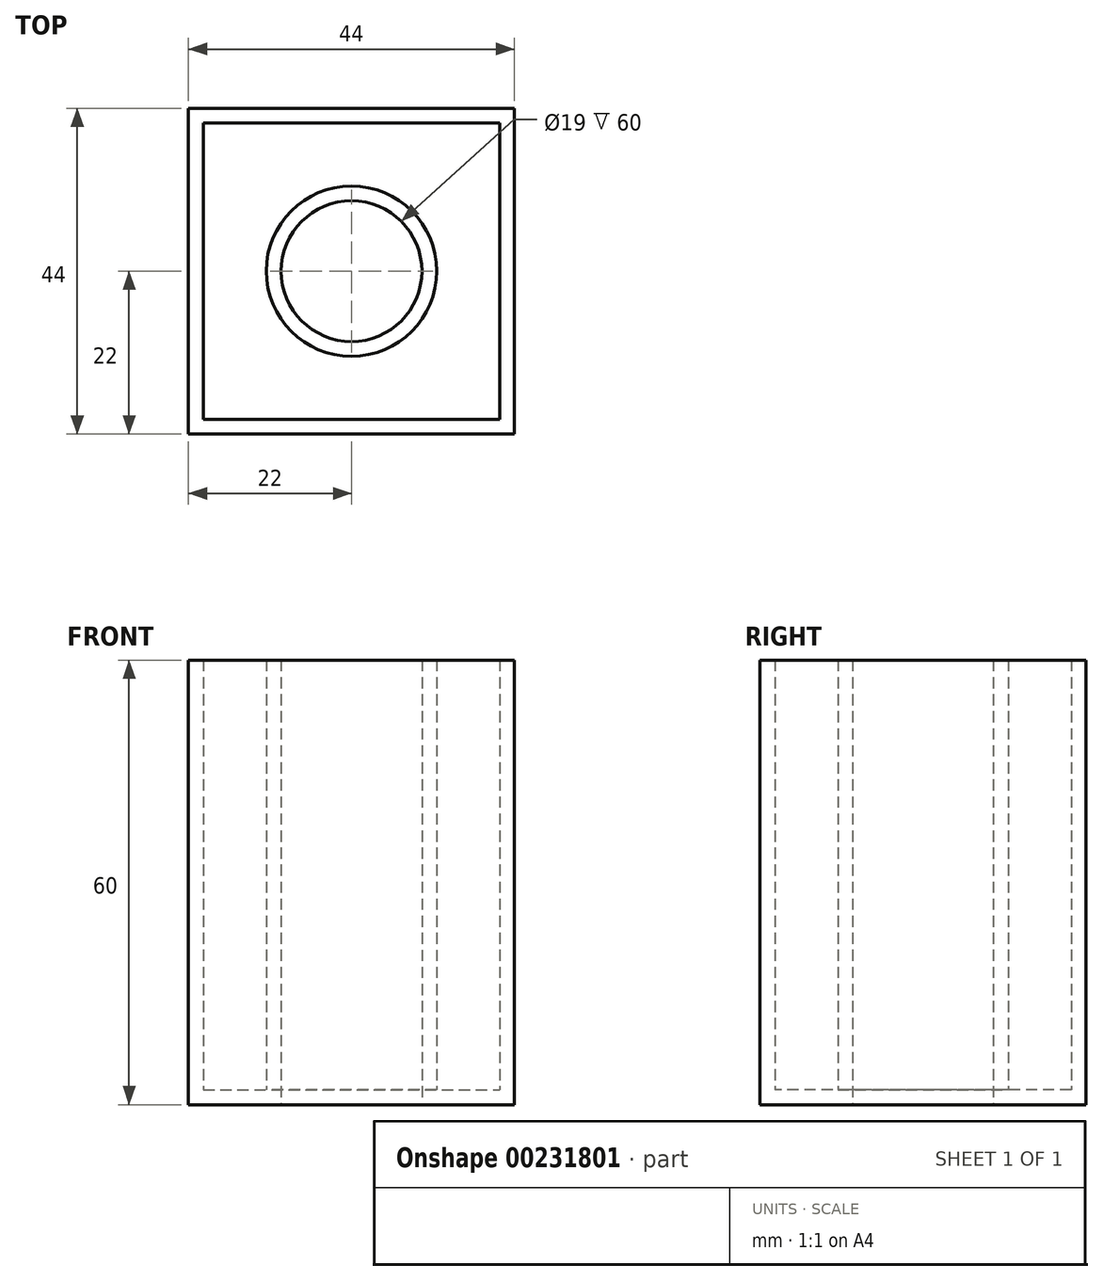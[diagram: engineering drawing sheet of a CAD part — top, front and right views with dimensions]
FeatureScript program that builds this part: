
annotation { "Feature Type Name" : "Feature", "Feature Type Description" : "" }
export const myFeature = defineFeature(function(context is Context, id is Id, definition is map)
    precondition{}
    {
        {
            var Q0;
            Q0=qCreatedBy(makeId("Top.planeOp"),FACE);
            var sketch = newSketch(context, id + "F0", { "sketchPlane" : qUnion([Q0])});
            skCircle(sketch, "E0", {"center": v(0, 0) * mm, "radius": 9.5 * mm});
            skLineSegment(sketch, "E1.bottom", {"start": v(-20, 20) * mm, "end": v(20, 20) * mm});
            skLineSegment(sketch, "E1.top", {"start": v(-20, -20) * mm, "end": v(20, -20) * mm});
            skLineSegment(sketch, "E1.left", {"start": v(-20, 20) * mm, "end": v(-20, -20) * mm});
            skLineSegment(sketch, "E1.right", {"start": v(20, 20) * mm, "end": v(20, -20) * mm});
            skLineSegment(sketch, "E2.bottom", {"start": v(-22, 22) * mm, "end": v(22, 22) * mm});
            skLineSegment(sketch, "E2.top", {"start": v(-22, -22) * mm, "end": v(22, -22) * mm});
            skLineSegment(sketch, "E2.left", {"start": v(-22, 22) * mm, "end": v(-22, -22) * mm});
            skLineSegment(sketch, "E2.right", {"start": v(22, 22) * mm, "end": v(22, -22) * mm});
            skCircle(sketch, "E3", {"center": v(0, 0) * mm, "radius": 11.5 * mm});
            skSolve(sketch);
        }
        {
            var Q0;
            Q0=makeQuery(id+"F0.imprint","IMPRINT",FACE,{"disambiguationData":[TD([[makeQuery(id+"F0.imprint","IMPRINT",EDGE,{"derivedFrom":sQuery(id+"F0.wireOp",EDGE,"E0")}),-1.0]])]});
            extrude(context, id + "F1", {"entities" : qUnion([Q0]), "depth" : 60 * mm});
        }
        {
            var Q0;
            Q0=makeQuery(id+"F0.imprint","IMPRINT",FACE,{"disambiguationData":[TD([[makeQuery(id+"F0.imprint","IMPRINT",EDGE,{"derivedFrom":sQuery(id+"F0.wireOp",EDGE,"E1.bottom")}),1.0]])]});
            extrude(context, id + "F2", {"entities" : qUnion([Q0]), "operationType" : NewBodyOperationType.ADD, "depth" : 60 * mm});
        }
        {
            var Q0;
            Q0=makeQuery(id+"F0.imprint","IMPRINT",FACE,{"disambiguationData":[TD([[makeQuery(id+"F0.imprint","IMPRINT",EDGE,{"derivedFrom":sQuery(id+"F0.wireOp",EDGE,"E1.bottom")}),-1.0]])]});
            extrude(context, id + "F3", {"entities" : qUnion([Q0]), "operationType" : NewBodyOperationType.ADD, "depth" : 2 * mm});
        }
    });
